# Revit family: 931-20-001 DN900
name_source: partatom
category: Pipe Accessories
units: mm (PartAtom-declared; Revit-internal decimal feet)

## family parameters
Always vertical = Yes
Cut with Voids When Loaded = No
Part Type = Valve - Breaks Into
Round Connector Dimension = Use Diameter
Shared = No
Work Plane-Based = No

## types (2) — shared parameters
1 = 1 mm  [stored 0.00328084 ft]
2 = 3 mm  [stored 0.00984252 ft]
Actuator_FL_T = 35 mm  [stored 0.114829 ft]
Actuator_Flange_R = 150 mm  [stored 0.492126 ft]
B = 450 mm  [stored 1.47638 ft]
B1 = 451 mm
Body_Thickness = 2 mm  [stored 0.00656168 ft]
Body_dim = 75 mm  [stored 0.246063 ft]
Body_dim1 = 140 mm  [stored 0.459318 ft]
Body_thickness = 473 mm
Bore_R = 450 mm  [stored 1.47638 ft]
C = 200 mm  [stored 0.656168 ft]
D = 524 mm  [stored 1.71916 ft]
DN = 900 mm  [stored 2.95276 ft]
DN900_PN10 = 931-900-20-010020200000
DN900_PN16 = 931-900-20-020020200000
Description_ = AVK BUTTERFLY VALVE, LUG, PN10/16
E = 705 mm  [stored 2.31299 ft]
F = 75 mm  [stored 0.246063 ft]
G = 55 mm  [stored 0.180446 ft]
H = 150 mm  [stored 0.492126 ft]
Hole = 61 mm
Hole1 = 34 mm  [stored 0.111549 ft]
PCD_R = 550 mm  [stored 1.80446 ft]
Search_table = 931-20-001 DN900
Slot_dim = 42 mm  [stored 0.137795 ft]
URL_product_pages = https://www.avkvalves.com
base = 70 mm  [stored 0.229659 ft]
base1 = 40 mm  [stored 0.131234 ft]
base_dis = 618 mm
disk = 30 mm  [stored 0.0984252 ft]
disk1 = 52 mm
disk11 = 68 mm  [stored 0.223097 ft]
disk2 = 899 mm  [stored 2.94948 ft]
disk22 = 39 mm  [stored 0.127953 ft]
hole1 = 28 mm  [stored 0.0918635 ft]
rubber = 37 mm  [stored 0.121391 ft]
support = 636 mm  [stored 2.08661 ft]
wafer = 225 mm  [stored 0.738189 ft]
wafer_F = 67 mm  [stored 0.219816 ft]
wafer_dim2 = 225 mm  [stored 0.738189 ft]
wafer_fillet = 113 mm
zero-valued in all types: DISK, Default Elevation

## per-type parameters (varying)
| type | Flange_R | Flange_T | wafer_dim1 |
| DN900_PN10 | 520 mm  [stored 1.70604 ft] | 38 mm  [stored 0.124672 ft] | 38 mm  [stored 0.124672 ft] |
| DN900_PN16 | 525 mm  [stored 1.72244 ft] | 47 mm | 47 mm |

note: [stored X ft] marks values corroborated as IEEE doubles in the binary element streams (Revit-internal decimal feet)

## geometry (parser evidence)
native form markers: Sweep x7
no freeform markers — native parametric forms only
